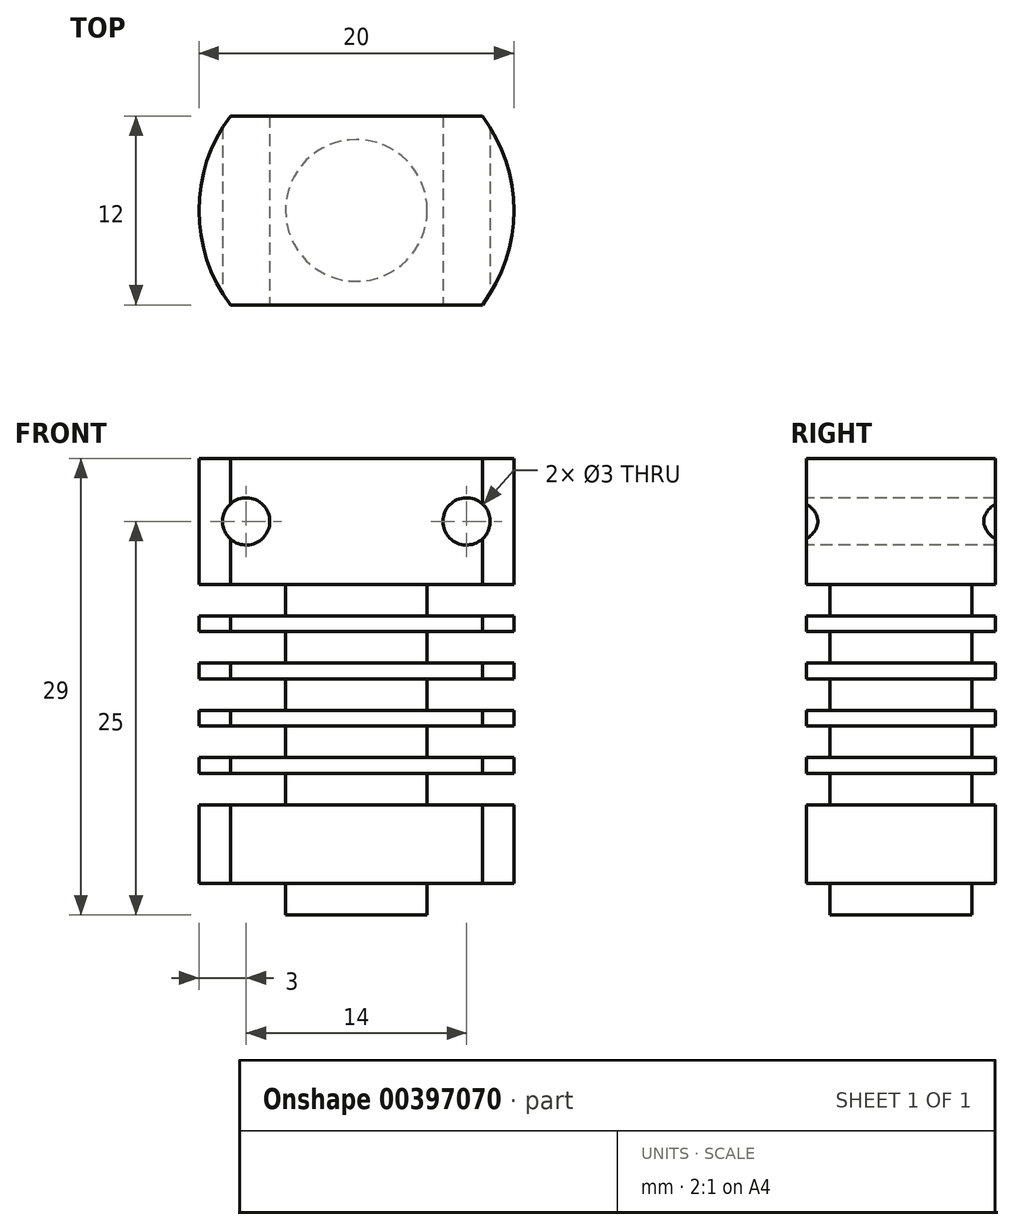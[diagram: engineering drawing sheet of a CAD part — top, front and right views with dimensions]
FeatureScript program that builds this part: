
annotation { "Feature Type Name" : "Feature", "Feature Type Description" : "" }
export const myFeature = defineFeature(function(context is Context, id is Id, definition is map)
    precondition{}
    {
        {
            var Q0;
            Q0=qCreatedBy(makeId("Top.planeOp"),FACE);
            var sketch = newSketch(context, id + "F0", { "sketchPlane" : qUnion([Q0])});
            skLineSegment(sketch, "E0.bottom", {"start": v(8, -6) * mm, "end": v(-8, -6) * mm});
            skLineSegment(sketch, "E0.top", {"start": v(8, 6) * mm, "end": v(-8, 6) * mm});
            skPoint(sketch, "E0.middle", {"position": v(0, 0) * mm});
            skArc(sketch, "E1", {"start": v(-8, 6) * mm, "mid": v(-10, 0) * mm, "end": v(-8, -6) * mm});
            skArc(sketch, "E2.trimOffspring", {"start": v(8, -6) * mm, "mid": v(10, 0) * mm, "end": v(8, 6) * mm});
            skPoint(sketch, "E3.orphan", {"position": v(-10, -6) * mm});
            skPoint(sketch, "E4.orphan", {"position": v(-10, 6) * mm});
            skPoint(sketch, "E5.orphan", {"position": v(10, 6) * mm});
            skPoint(sketch, "E6.orphan", {"position": v(10, -6) * mm});
            skSolve(sketch);
        }
        {
            var Q0;
            Q0=makeQuery(id+"F0.imprint","IMPRINT",FACE,{"disambiguationData":[TD([[makeQuery(id+"F0.imprint","IMPRINT",EDGE,{"derivedFrom":sQuery(id+"F0.wireOp",EDGE,"E0.bottom")}),-1.0]])]});
            extrude(context, id + "F1", {"entities" : qUnion([Q0]), "depth" : 27 * mm});
        }
        {
            var Q0;
            Q0=qCreatedBy(makeId("Front.planeOp"),FACE);
            var sketch = newSketch(context, id + "F2", { "sketchPlane" : qUnion([Q0])});
            skLineSegment(sketch, "E7.bottom", {"start": v(15, 5) * mm, "end": v(-15, 5) * mm});
            skLineSegment(sketch, "E7.top", {"start": v(15, 7) * mm, "end": v(-15, 7) * mm});
            skLineSegment(sketch, "E7.left", {"start": v(15, 5) * mm, "end": v(15, 7) * mm});
            skLineSegment(sketch, "E7.right", {"start": v(-15, 5) * mm, "end": v(-15, 7) * mm});
            skPoint(sketch, "E7.middle", {"position": v(0, 6) * mm});
            skLineSegment(sketch, "E8.0.1.0", {"start": v(15, 10) * mm, "end": v(-15, 10) * mm});
            skLineSegment(sketch, "E8.0.1.1", {"start": v(15, 8) * mm, "end": v(-15, 8) * mm});
            skPoint(sketch, "E8.0.1.2", {"position": v(0, 9) * mm});
            skLineSegment(sketch, "E8.0.1.3", {"start": v(-15, 8) * mm, "end": v(-15, 10) * mm});
            skLineSegment(sketch, "E8.0.1.4", {"start": v(15, 8) * mm, "end": v(15, 10) * mm});
            skLineSegment(sketch, "E8.0.2.0", {"start": v(15, 13) * mm, "end": v(-15, 13) * mm});
            skLineSegment(sketch, "E8.0.2.1", {"start": v(15, 11) * mm, "end": v(-15, 11) * mm});
            skPoint(sketch, "E8.0.2.2", {"position": v(0, 12) * mm});
            skLineSegment(sketch, "E8.0.2.3", {"start": v(-15, 11) * mm, "end": v(-15, 13) * mm});
            skLineSegment(sketch, "E8.0.2.4", {"start": v(15, 11) * mm, "end": v(15, 13) * mm});
            skLineSegment(sketch, "E8.0.3.0", {"start": v(15, 16) * mm, "end": v(-15, 16) * mm});
            skLineSegment(sketch, "E8.0.3.1", {"start": v(15, 14) * mm, "end": v(-15, 14) * mm});
            skPoint(sketch, "E8.0.3.2", {"position": v(0, 15) * mm});
            skLineSegment(sketch, "E8.0.3.3", {"start": v(-15, 14) * mm, "end": v(-15, 16) * mm});
            skLineSegment(sketch, "E8.0.3.4", {"start": v(15, 14) * mm, "end": v(15, 16) * mm});
            skLineSegment(sketch, "E8.0.4.0", {"start": v(15, 19) * mm, "end": v(-15, 19) * mm});
            skLineSegment(sketch, "E8.0.4.1", {"start": v(15, 17) * mm, "end": v(-15, 17) * mm});
            skPoint(sketch, "E8.0.4.2", {"position": v(0, 18) * mm});
            skLineSegment(sketch, "E8.0.4.3", {"start": v(-15, 17) * mm, "end": v(-15, 19) * mm});
            skLineSegment(sketch, "E8.0.4.4", {"start": v(15, 17) * mm, "end": v(15, 19) * mm});
            skLineSegment(sketch, "E8.direction1", {"start": v(-15, 5) * mm, "end": v(10, 5) * mm, "construction": true});
            skLineSegment(sketch, "E8.direction2", {"start": v(-15, 5) * mm, "end": v(-15, 8) * mm, "construction": true});
            skSolve(sketch);
        }
        {
            var Q0;
            Q0=qSketchRegion(id+"F2",true);
            extrude(context, id + "F3", {"entities" : qUnion([Q0]), "operationType" : NewBodyOperationType.REMOVE, "endBound" : BoundingType.SYMMETRIC, "oppositeDirection" : true, "depth" : 12 * mm});
        }
        {
            var Q0;
            Q0=qCreatedBy(makeId("Top.planeOp"),FACE);
            var sketch = newSketch(context, id + "F4", { "sketchPlane" : qUnion([Q0])});
            skCircle(sketch, "E9", {"center": v(0, 0) * mm, "radius": 4.5 * mm});
            skSolve(sketch);
        }
        {
            var Q0;
            Q0=makeQuery(id+"F4.imprint","IMPRINT",FACE,{"disambiguationData":[TD([[makeQuery(id+"F4.imprint","IMPRINT",EDGE,{"derivedFrom":sQuery(id+"F4.wireOp",EDGE,"E9")}),1.0]])]});
            var Q1;
            Q1=sQuery(id+"F4.wireOp",EDGE,"E9");
            extrude(context, id + "F5", {"entities" : qUnion([Q0]), "operationType" : NewBodyOperationType.ADD, "surfaceEntities" : qUnion([Q1]), "depth" : 27 * mm, "hasSecondDirection" : true, "secondDirectionOppositeDirection" : true, "secondDirectionDepth" : 2 * mm});
        }
        {
            var Q0;
            Q0=qCreatedBy(makeId("Front.planeOp"),FACE);
            var sketch = newSketch(context, id + "F6", { "sketchPlane" : qUnion([Q0])});
            skCircle(sketch, "E10", {"center": v(-7, 23) * mm, "radius": 1.5 * mm});
            skCircle(sketch, "E11.MirrorC", {"center": v(7, 23) * mm, "radius": 1.5 * mm});
            skSolve(sketch);
        }
        {
            var Q0;
            Q0=qSketchRegion(id+"F6",true);
            extrude(context, id + "F7", {"entities" : qUnion([Q0]), "operationType" : NewBodyOperationType.REMOVE, "endBound" : BoundingType.SYMMETRIC, "oppositeDirection" : true, "depth" : 12 * mm});
        }
    });
